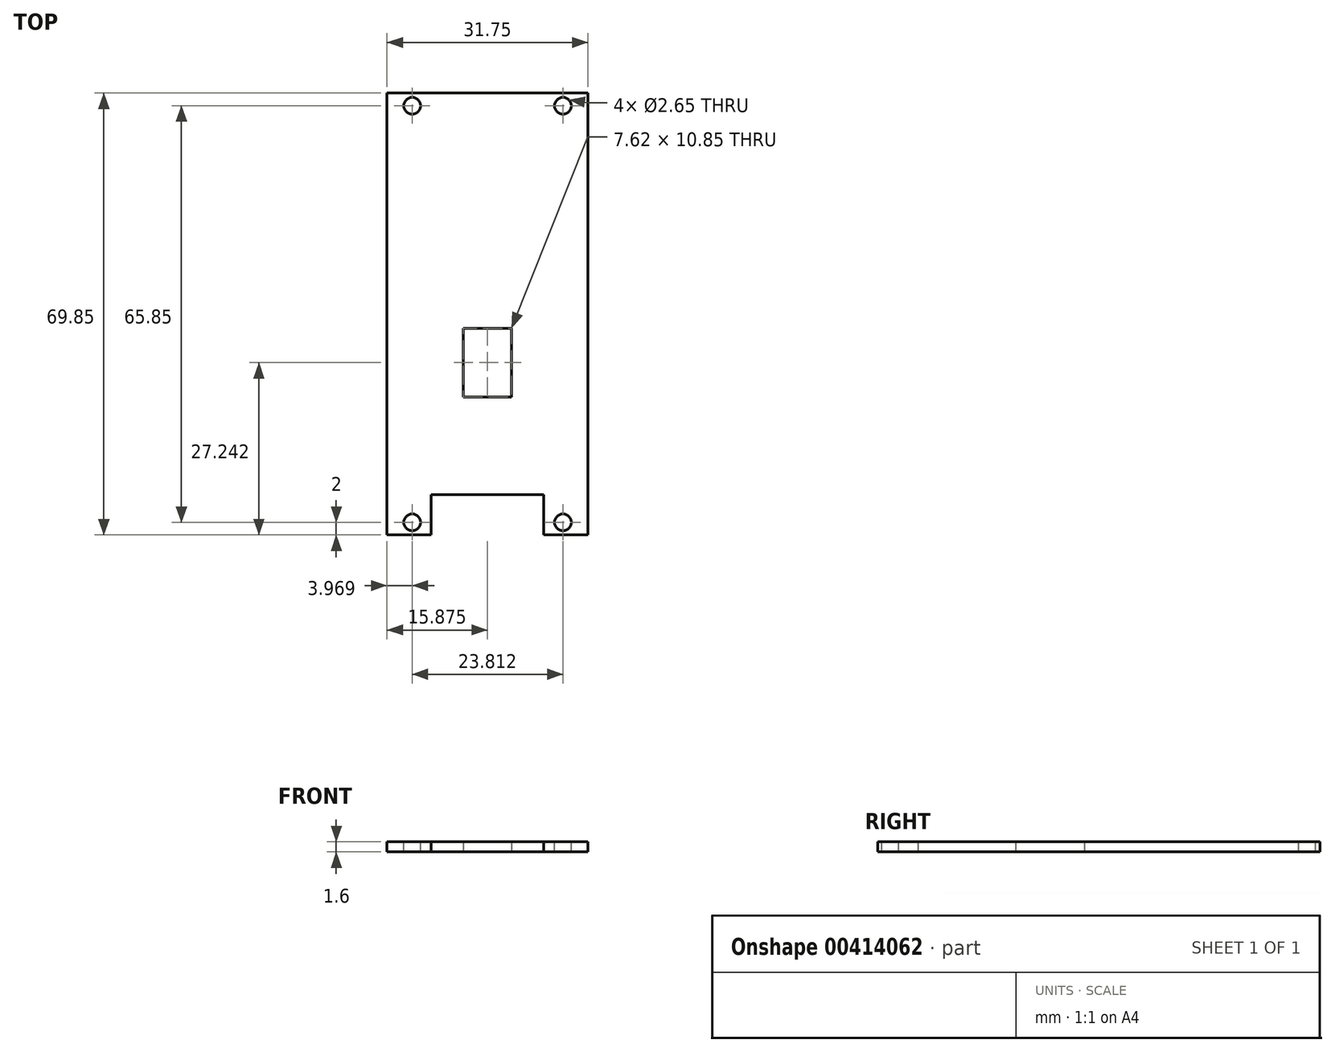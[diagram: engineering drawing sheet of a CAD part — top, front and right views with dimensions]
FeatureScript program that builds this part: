
annotation { "Feature Type Name" : "Feature", "Feature Type Description" : "" }
export const myFeature = defineFeature(function(context is Context, id is Id, definition is map)
    precondition{}
    {
        {
            var Q0;
            Q0=qCreatedBy(makeId("Top.planeOp"),FACE);
            var sketch = newSketch(context, id + "F0", { "sketchPlane" : qUnion([Q0])});
            skLineSegment(sketch, "E0.bottom", {"start": v(0, 0) * mm, "end": v(31.75, 0) * mm});
            skLineSegment(sketch, "E0.top", {"start": v(0, 63.5) * mm, "end": v(31.75, 63.5) * mm});
            skLineSegment(sketch, "E0.left", {"start": v(0, 0) * mm, "end": v(0, 63.5) * mm});
            skLineSegment(sketch, "E0.right", {"start": v(31.75, 0) * mm, "end": v(31.75, 63.5) * mm});
            skPoint(sketch, "E1.middle", {"position": v(15.87, 31.75) * mm});
            skLineSegment(sketch, "E2", {"start": v(12.06, 15.47) * mm, "end": v(19.68, 15.47) * mm});
            skLineSegment(sketch, "E3", {"start": v(19.68, 15.47) * mm, "end": v(19.68, 26.32) * mm});
            skLineSegment(sketch, "E4", {"start": v(19.68, 26.32) * mm, "end": v(12.06, 26.32) * mm});
            skLineSegment(sketch, "E5", {"start": v(12.06, 26.32) * mm, "end": v(12.06, 15.47) * mm});
            skPoint(sketch, "E6.orphan", {"position": v(15.87, 63.5) * mm});
            skPoint(sketch, "E7.orphan", {"position": v(19.68, 50.8) * mm});
            skPoint(sketch, "E8.orphan", {"position": v(12.06, 50.8) * mm});
            skPoint(sketch, "E9.orphan", {"position": v(12.06, 12.7) * mm});
            skPoint(sketch, "E1.top.start.orphan", {"position": v(19.68, 12.7) * mm});
            skPoint(sketch, "E10.trimOffspring.end.orphan", {"position": v(15.88, 0) * mm});
            skSolve(sketch);
        }
        {
            var Q0;
            Q0=makeQuery(id+"F0.imprint","IMPRINT",FACE,{"disambiguationData":[TD([[makeQuery(id+"F0.imprint","IMPRINT",EDGE,{"derivedFrom":sQuery(id+"F0.wireOp",EDGE,"E0.bottom")}),1.0]])]});
            extrude(context, id + "F1", {"entities" : qUnion([Q0]), "depth" : 1.6 * mm});
        }
        {
            var Q0;
            Q0=makeQuery(id+"F1.opExtrude","SWEPT_FACE",FACE,{"disambiguationData":[OSD([sQuery(id+"F0.wireOp",EDGE,"E0.bottom")])]});
            var sketch = newSketch(context, id + "F2", { "sketchPlane" : qUnion([Q0])});
            skLineSegment(sketch, "E11", {"start": v(15.87, 1.6) * mm, "end": v(15.87, 0) * mm});
            skLineSegment(sketch, "E12.bottom", {"start": v(24.77, 1.6) * mm, "end": v(6.98, 1.6) * mm});
            skLineSegment(sketch, "E12.top", {"start": v(24.76, 0) * mm, "end": v(6.98, 0) * mm});
            skLineSegment(sketch, "E12.left", {"start": v(24.76, 1.6) * mm, "end": v(24.76, 0) * mm});
            skLineSegment(sketch, "E12.right", {"start": v(6.98, 1.6) * mm, "end": v(6.98, 0) * mm});
            skPoint(sketch, "E12.middle", {"position": v(15.87, 0.8) * mm});
            skSolve(sketch);
        }
        {
            var Q0;
            {var subQ0=sQuery(id+"F2.wireOp",EDGE,"E12.right");Q0=makeQuery(id+"F2.imprint","IMPRINT",FACE,{"disambiguationData":[TD([[makeQuery(id+"F2.imprint","IMPRINT",EDGE,{"derivedFrom":subQ0}),-1.0]])]});}
            var Q1;
            {var subQ0=sQuery(id+"F2.wireOp",EDGE,"E12.left");Q1=makeQuery(id+"F2.imprint","IMPRINT",FACE,{"disambiguationData":[TD([[makeQuery(id+"F2.imprint","IMPRINT",EDGE,{"derivedFrom":subQ0}),1.0]])]});}
            extrude(context, id + "F3", {"entities" : qUnion([Q0, Q1]), "operationType" : NewBodyOperationType.ADD, "depth" : 6.35 * mm});
        }
        {
            var Q0;
            {var subQ0=sQuery(id+"F0.wireOp",EDGE,"E0.bottom");var subQ1=makeQuery(id+"F1.opExtrude","CAP_EDGE",EDGE,{"disambiguationData":[OSD([subQ0])],"isStart":false});var subQ2=sQuery(id+"F0.wireOp",EDGE,"E0.right");var subQ4=sQuery(id+"F0.wireOp",EDGE,"E0.left");Q0=makeQuery(id+"F3.boolean.opBoolean","MERGE",FACE,{"derivedFrom":[makeQuery(id+"F1.opExtrude","CAP_FACE",FACE,{"disambiguationData":[OSD([subQ0,sQuery(id+"F0.wireOp",EDGE,"E0.top"),subQ4,subQ2])],"isStart":false}),makeQuery(id+"F3.opExtrude","SWEPT_FACE",FACE,{"disambiguationData":[OSD([subQ0]),TDD([makeQuery(id+"F2.imprint","IMPRINT",EDGE,{"disambiguationData":[TD([[makeQuery(id+"F2.imprint","INTERSECT",VERTEX,{"derivedFrom":[makeQuery(id+"F1.opExtrude","SWEPT_EDGE",EDGE,{"disambiguationData":[OSD([subQ0,subQ4])]}),subQ1]}),-1.0]])],"derivedFrom":subQ1})])]}),makeQuery(id+"F3.opExtrude","SWEPT_FACE",FACE,{"disambiguationData":[OSD([subQ0]),TDD([makeQuery(id+"F2.imprint","IMPRINT",EDGE,{"disambiguationData":[TD([[makeQuery(id+"F2.imprint","INTERSECT",VERTEX,{"derivedFrom":[makeQuery(id+"F1.opExtrude","SWEPT_EDGE",EDGE,{"disambiguationData":[OSD([subQ0,subQ2])]}),subQ1]}),1.0]])],"derivedFrom":subQ1})])]})]});}
            var sketch = newSketch(context, id + "F4", { "sketchPlane" : qUnion([Q0])});
            skLineSegment(sketch, "E13", {"start": v(3.97, -6.35) * mm, "end": v(3.97, -4.35) * mm});
            skLineSegment(sketch, "E14", {"start": v(3.97, -4.35) * mm, "end": v(27.78, -4.35) * mm});
            skLineSegment(sketch, "E15", {"start": v(27.78, -5.68) * mm, "end": v(27.78, -6.35) * mm});
            skPoint(sketch, "E16.end.orphan", {"position": v(3.5, 0) * mm});
            skPoint(sketch, "E16.start.orphan", {"position": v(3.5, -6.35) * mm});
            skPoint(sketch, "E17.end.orphan", {"position": v(28.26, 0) * mm});
            skPoint(sketch, "E17.start.orphan", {"position": v(28.26, -6.35) * mm});
            skLineSegment(sketch, "E18", {"start": v(15.87, 0) * mm, "end": v(15.87, -4.35) * mm});
            skCircle(sketch, "E19", {"center": v(3.97, -4.35) * mm, "radius": 1.32 * mm});
            skCircle(sketch, "E20", {"center": v(27.78, -4.35) * mm, "radius": 1.32 * mm});
            skLineSegment(sketch, "E21", {"start": v(27.78, -4.35) * mm, "end": v(27.78, -3.03) * mm});
            skLineSegment(sketch, "E22", {"start": v(3.97, 61.5) * mm, "end": v(27.78, 61.5) * mm});
            skCircle(sketch, "E23", {"center": v(3.97, 61.5) * mm, "radius": 1.32 * mm});
            skCircle(sketch, "E24", {"center": v(27.78, 61.5) * mm, "radius": 1.32 * mm});
            skLineSegment(sketch, "E25.trimOffspring", {"start": v(3.97, 62.82) * mm, "end": v(3.97, 63.5) * mm});
            skSolve(sketch);
        }
        {
            var Q0;
            {var subQ0=sQuery(id+"F4.wireOp",EDGE,"E14");var subQ1=sQuery(id+"F4.wireOp",EDGE,"E13");var subQ2=makeQuery(id+"F4.imprint","INTERSECT",VERTEX,{"derivedFrom":[subQ1,subQ0]});Q0=makeQuery(id+"F4.imprint","IMPRINT",FACE,{"disambiguationData":[TD([[makeQuery(id+"F4.imprint","IMPRINT",EDGE,{"disambiguationData":[TD([[subQ2,1.0]])],"derivedFrom":subQ1}),1.0]])]});}
            var Q1;
            {var subQ0=sQuery(id+"F4.wireOp",EDGE,"E14");var subQ1=sQuery(id+"F4.wireOp",EDGE,"E13");var subQ2=makeQuery(id+"F4.imprint","INTERSECT",VERTEX,{"derivedFrom":[subQ1,subQ0]});Q1=makeQuery(id+"F4.imprint","IMPRINT",FACE,{"disambiguationData":[TD([[makeQuery(id+"F4.imprint","IMPRINT",EDGE,{"disambiguationData":[TD([[subQ2,1.0]])],"derivedFrom":subQ1}),-1.0]])]});}
            var Q2;
            {var subQ0=sQuery(id+"F4.wireOp",EDGE,"E15");var subQ1=sQuery(id+"F4.wireOp",EDGE,"E14");var subQ2=makeQuery(id+"F4.imprint","INTERSECT",VERTEX,{"derivedFrom":[subQ1,subQ0]});Q2=makeQuery(id+"F4.imprint","IMPRINT",FACE,{"disambiguationData":[TD([[makeQuery(id+"F4.imprint","IMPRINT",EDGE,{"disambiguationData":[TD([[subQ2,1.0]])],"derivedFrom":subQ1}),1.0]])]});}
            var Q3;
            {var subQ0=sQuery(id+"F4.wireOp",EDGE,"E15");var subQ1=sQuery(id+"F4.wireOp",EDGE,"E14");var subQ2=makeQuery(id+"F4.imprint","INTERSECT",VERTEX,{"derivedFrom":[subQ1,subQ0]});Q3=makeQuery(id+"F4.imprint","IMPRINT",FACE,{"disambiguationData":[TD([[makeQuery(id+"F4.imprint","IMPRINT",EDGE,{"disambiguationData":[TD([[subQ2,1.0]])],"derivedFrom":subQ1}),-1.0]])]});}
            extrude(context, id + "F5", {"entities" : qUnion([Q0, Q1, Q2, Q3]), "operationType" : NewBodyOperationType.REMOVE, "oppositeDirection" : true, "depth" : 25.4 * mm});
        }
        {
            var Q0;
            {var subQ0=sQuery(id+"F4.wireOp",EDGE,"E21");Q0=makeQuery(id+"F4.imprint","IMPRINT",FACE,{"disambiguationData":[TD([[makeQuery(id+"F4.imprint","IMPRINT",EDGE,{"derivedFrom":subQ0}),-1.0]])]});}
            var Q1;
            Q1=makeQuery(id+"F4.imprint","IMPRINT",FACE,{"disambiguationData":[TD([[makeQuery(id+"F4.imprint","IMPRINT",EDGE,{"derivedFrom":sQuery(id+"F4.wireOp",EDGE,"E24")}),1.0]])]});
            var Q2;
            {var subQ0=sQuery(id+"F4.wireOp",EDGE,"E23");var subQ1=makeQuery(id+"F4.imprint","IMPRINT",VERTEX,{"disambiguationData":[OD(0.0)],"derivedFrom":subQ0});Q2=makeQuery(id+"F4.imprint","IMPRINT",FACE,{"disambiguationData":[TD([[makeQuery(id+"F4.imprint","IMPRINT",EDGE,{"disambiguationData":[TD([[subQ1,1.0]])],"derivedFrom":subQ0}),1.0]])]});}
            extrude(context, id + "F6", {"entities" : qUnion([Q0, Q1, Q2]), "operationType" : NewBodyOperationType.REMOVE, "oppositeDirection" : true, "depth" : 25.4 * mm});
        }
    });
